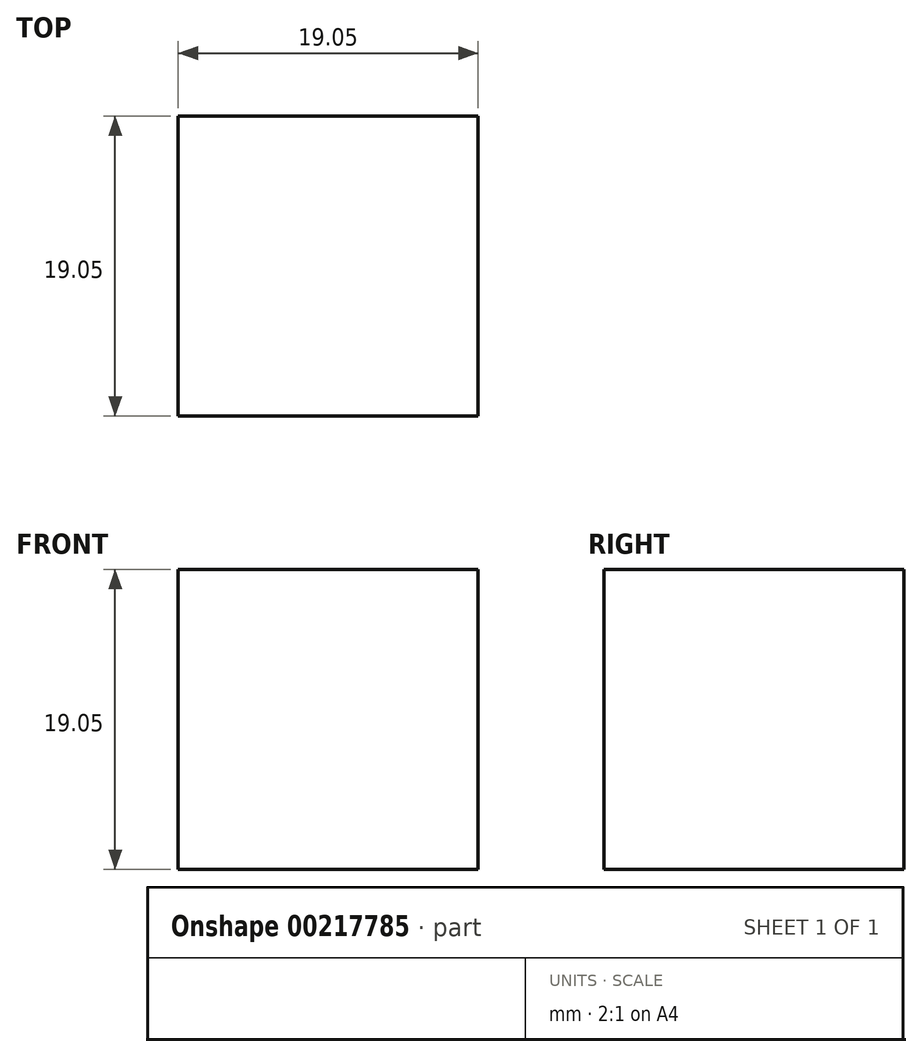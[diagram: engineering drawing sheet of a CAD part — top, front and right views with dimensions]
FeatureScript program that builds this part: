
annotation { "Feature Type Name" : "Feature", "Feature Type Description" : "" }
export const myFeature = defineFeature(function(context is Context, id is Id, definition is map)
    precondition{}
    {
        {
            var Q0;
            Q0=qCreatedBy(makeId("Front.planeOp"),FACE);
            var sketch = newSketch(context, id + "F0", { "sketchPlane" : qUnion([Q0])});
            skLineSegment(sketch, "E0.bottom", {"start": v(-35.74, 47.1) * mm, "end": v(-16.7, 47.1) * mm});
            skLineSegment(sketch, "E0.top", {"start": v(-35.74, 28.05) * mm, "end": v(-16.7, 28.05) * mm});
            skLineSegment(sketch, "E0.left", {"start": v(-35.74, 47.1) * mm, "end": v(-35.74, 28.05) * mm});
            skLineSegment(sketch, "E0.right", {"start": v(-16.7, 47.1) * mm, "end": v(-16.7, 28.05) * mm});
            skSolve(sketch);
        }
        {
            var Q0;
            Q0 = qSketchRegion(id + "F0", true);
            extrude(context, id + "F1", {"entities" : qUnion([Q0]), "depth" : 19.05 * mm});
        }
    });
